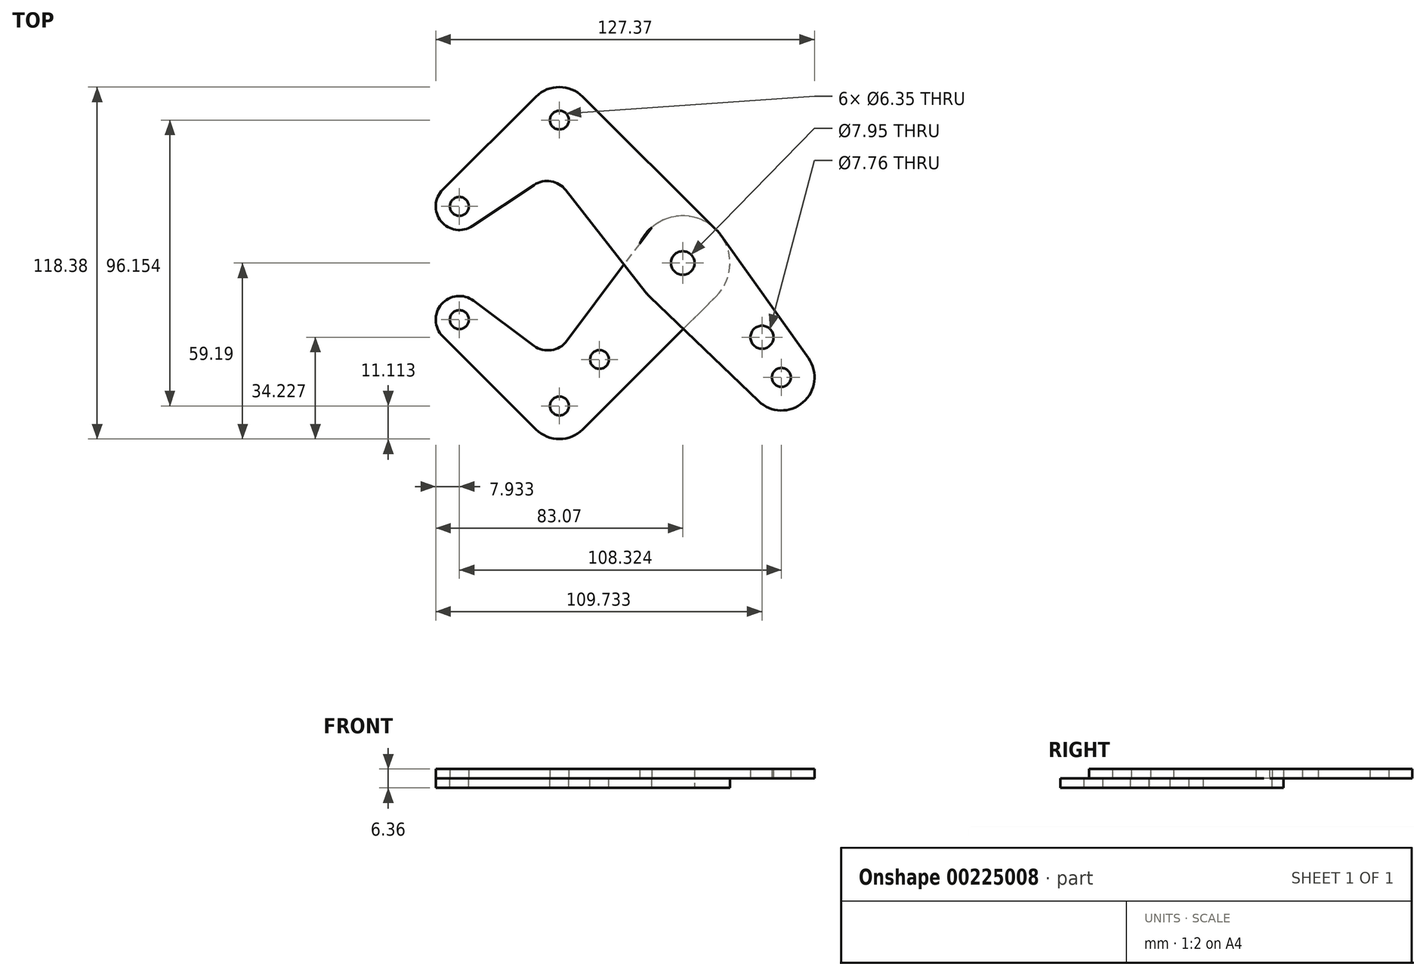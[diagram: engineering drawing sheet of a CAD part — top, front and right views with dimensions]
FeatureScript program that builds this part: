
annotation { "Feature Type Name" : "Feature", "Feature Type Description" : "" }
export const myFeature = defineFeature(function(context is Context, id is Id, definition is map)
    precondition{}
    {
        {
            var Q0;
            Q0=qCreatedBy(makeId("Top.planeOp"),FACE);
            var sketch = newSketch(context, id + "F0", { "sketchPlane" : qUnion([Q0])});
            skCircle(sketch, "E0", {"center": v(0, 0) * mm, "radius": 15.88 * mm});
            skCircle(sketch, "E1", {"center": v(0, 0) * mm, "radius": 3.98 * mm});
            skLineSegment(sketch, "E2", {"start": v(0, 0) * mm, "end": v(-41.48, 48.08) * mm, "construction": true});
            skCircle(sketch, "E3", {"center": v(-41.48, 48.08) * mm, "radius": 11.11 * mm});
            skLineSegment(sketch, "E4", {"start": v(-33.64, 55.95) * mm, "end": v(11.2, 11.24) * mm});
            skLineSegment(sketch, "E5", {"start": v(-41.48, 48.08) * mm, "end": v(-75.14, 19.04) * mm, "construction": true});
            skCircle(sketch, "E6", {"center": v(-75.14, 19.04) * mm, "radius": 7.94 * mm});
            skCircle(sketch, "E7", {"center": v(-41.48, 48.08) * mm, "radius": 3.18 * mm});
            skCircle(sketch, "E8", {"center": v(-75.14, 19.04) * mm, "radius": 3.18 * mm});
            skLineSegment(sketch, "E9", {"start": v(-80.74, 24.66) * mm, "end": v(-49.33, 55.95) * mm});
            skLineSegment(sketch, "E10", {"start": v(-70.74, 12.43) * mm, "end": v(-49.99, 26.24) * mm});
            skLineSegment(sketch, "E11", {"start": v(-12.5, -9.78) * mm, "end": v(-39.32, 24.52) * mm});
            skPoint(sketch, "E12.visualSharp", {"position": v(-43.86, 30.32) * mm});
            skArc(sketch, "E12.filletArc", {"start": v(-39.32, 24.52) * mm, "mid": v(-44.32, 27.47) * mm, "end": v(-49.99, 26.24) * mm});
            skLineSegment(sketch, "E13", {"start": v(0, 0) * mm, "end": v(33.19, -38.46) * mm, "construction": true});
            skCircle(sketch, "E14", {"center": v(0, 0) * mm, "radius": 3.18 * mm});
            skCircle(sketch, "E15", {"center": v(33.19, -38.46) * mm, "radius": 11.11 * mm});
            skCircle(sketch, "E16", {"center": v(33.19, -38.46) * mm, "radius": 3.18 * mm});
            skCircle(sketch, "E17", {"center": v(26.66, -24.96) * mm, "radius": 3.88 * mm});
            skLineSegment(sketch, "E18", {"start": v(12.94, 9.2) * mm, "end": v(42.24, -32.02) * mm});
            skLineSegment(sketch, "E19", {"start": v(-11, -11.45) * mm, "end": v(25.5, -46.48) * mm});
            skLineSegment(sketch, "E20", {"start": v(0, 0) * mm, "end": v(-41.48, -48.08) * mm, "construction": true});
            skCircle(sketch, "E21", {"center": v(-41.48, -48.08) * mm, "radius": 11.11 * mm});
            skCircle(sketch, "E22", {"center": v(-41.48, -48.08) * mm, "radius": 3.18 * mm});
            skCircle(sketch, "E23", {"center": v(-28, -32.44) * mm, "radius": 4.78 * mm});
            skLineSegment(sketch, "E24", {"start": v(-33.64, -55.95) * mm, "end": v(11.2, -11.24) * mm});
            skLineSegment(sketch, "E25", {"start": v(-41.48, -48.08) * mm, "end": v(-75.14, -19.04) * mm, "construction": true});
            skCircle(sketch, "E26", {"center": v(-75.14, -19.04) * mm, "radius": 7.94 * mm});
            skCircle(sketch, "E27", {"center": v(-75.14, -19.04) * mm, "radius": 3.18 * mm});
            skLineSegment(sketch, "E28", {"start": v(-80.74, -24.66) * mm, "end": v(-49.33, -55.95) * mm});
            skLineSegment(sketch, "E29", {"start": v(-10.37, 12.02) * mm, "end": v(-38.98, -26.2) * mm});
            skLineSegment(sketch, "E30", {"start": v(-70.4, -12.67) * mm, "end": v(-50.1, -27.8) * mm});
            skLineSegment(sketch, "E31.trimOffspring", {"start": v(-49.92, -40.8) * mm, "end": v(-50.38, -41.42) * mm});
            skLineSegment(sketch, "E32.trimOffspring", {"start": v(-34.84, -39.17) * mm, "end": v(-34.2, -39.64) * mm});
            skPoint(sketch, "E33.visualSharp", {"position": v(-43.73, -32.54) * mm});
            skArc(sketch, "E33.filletArc", {"start": v(-50.1, -27.8) * mm, "mid": v(-44.2, -29.3) * mm, "end": v(-38.98, -26.2) * mm});
            skLineSegment(sketch, "E34", {"start": v(-75.14, -19.04) * mm, "end": v(-75.14, 19.04) * mm, "construction": true});
            skCircle(sketch, "E35", {"center": v(-28, -32.44) * mm, "radius": 3.18 * mm});
            skSolve(sketch);
        }
        {
            var Q0;
            {var subQ0=sQuery(id+"F0.wireOp",EDGE,"E4");Q0=makeQuery(id+"F0.imprint","IMPRINT",FACE,{"disambiguationData":[TD([[makeQuery(id+"F0.imprint","IMPRINT",EDGE,{"derivedFrom":subQ0}),-1.0]])]});}
            var Q1;
            {var subQ0=sQuery(id+"F0.wireOp",EDGE,"E17");Q1=makeQuery(id+"F0.imprint","IMPRINT",FACE,{"disambiguationData":[TD([[makeQuery(id+"F0.imprint","IMPRINT",EDGE,{"derivedFrom":subQ0}),-1.0]])]});}
            var Q2;
            {var subQ0=sQuery(id+"F0.wireOp",EDGE,"E19");var subQ1=sQuery(id+"F0.wireOp",EDGE,"E0");var subQ2=makeQuery(id+"F0.imprint","INTERSECT",VERTEX,{"derivedFrom":[subQ1,subQ0]});Q2=makeQuery(id+"F0.imprint","IMPRINT",FACE,{"disambiguationData":[TD([[makeQuery(id+"F0.imprint","IMPRINT",EDGE,{"disambiguationData":[TD([[subQ2,-1.0]])],"derivedFrom":subQ1}),-1.0]])]});}
            var Q3;
            {var subQ0=sQuery(id+"F0.wireOp",EDGE,"E11");var subQ1=sQuery(id+"F0.wireOp",EDGE,"E0");var subQ2=makeQuery(id+"F0.imprint","INTERSECT",VERTEX,{"derivedFrom":[subQ1,subQ0]});Q3=makeQuery(id+"F0.imprint","IMPRINT",FACE,{"disambiguationData":[TD([[makeQuery(id+"F0.imprint","IMPRINT",EDGE,{"disambiguationData":[TD([[subQ2,1.0]])],"derivedFrom":subQ1}),-1.0]])]});}
            var Q4;
            Q4=makeQuery(id+"F0.imprint","IMPRINT",FACE,{"disambiguationData":[TD([[makeQuery(id+"F0.imprint","IMPRINT",EDGE,{"derivedFrom":sQuery(id+"F0.wireOp",EDGE,"E8")}),-1.0]])]});
            var Q5;
            Q5=makeQuery(id+"F0.imprint","IMPRINT",FACE,{"disambiguationData":[TD([[makeQuery(id+"F0.imprint","IMPRINT",EDGE,{"derivedFrom":sQuery(id+"F0.wireOp",EDGE,"E7")}),-1.0]])]});
            var Q6;
            Q6=makeQuery(id+"F0.imprint","IMPRINT",FACE,{"disambiguationData":[TD([[makeQuery(id+"F0.imprint","IMPRINT",EDGE,{"derivedFrom":sQuery(id+"F0.wireOp",EDGE,"E1")}),-1.0]])]});
            var Q7;
            Q7=makeQuery(id+"F0.imprint","IMPRINT",FACE,{"disambiguationData":[TD([[makeQuery(id+"F0.imprint","IMPRINT",EDGE,{"derivedFrom":sQuery(id+"F0.wireOp",EDGE,"E16")}),-1.0]])]});
            extrude(context, id + "F1", {"entities" : qUnion([Q0, Q1, Q2, Q3, Q4, Q5, Q6, Q7]), "depth" : 3.17 * mm});
        }
        {
            var Q0;
            Q0=makeQuery(id+"F0.imprint","IMPRINT",FACE,{"disambiguationData":[TD([[makeQuery(id+"F0.imprint","IMPRINT",EDGE,{"derivedFrom":sQuery(id+"F0.wireOp",EDGE,"E23")}),-1.0]])]});
            var Q1;
            {var subQ0=sQuery(id+"F0.wireOp",EDGE,"E19");var subQ1=sQuery(id+"F0.wireOp",EDGE,"E0");var subQ2=makeQuery(id+"F0.imprint","INTERSECT",VERTEX,{"derivedFrom":[subQ1,subQ0]});Q1=makeQuery(id+"F0.imprint","IMPRINT",FACE,{"disambiguationData":[TD([[makeQuery(id+"F0.imprint","IMPRINT",EDGE,{"disambiguationData":[TD([[subQ2,-1.0]])],"derivedFrom":subQ1}),-1.0]])]});}
            var Q2;
            {var subQ0=sQuery(id+"F0.wireOp",EDGE,"E11");var subQ1=sQuery(id+"F0.wireOp",EDGE,"E0");var subQ2=makeQuery(id+"F0.imprint","INTERSECT",VERTEX,{"derivedFrom":[subQ1,subQ0]});Q2=makeQuery(id+"F0.imprint","IMPRINT",FACE,{"disambiguationData":[TD([[makeQuery(id+"F0.imprint","IMPRINT",EDGE,{"disambiguationData":[TD([[subQ2,1.0]])],"derivedFrom":subQ1}),-1.0]])]});}
            var Q3;
            Q3=makeQuery(id+"F0.imprint","IMPRINT",FACE,{"disambiguationData":[TD([[makeQuery(id+"F0.imprint","IMPRINT",EDGE,{"derivedFrom":sQuery(id+"F0.wireOp",EDGE,"E1")}),-1.0]])]});
            var Q4;
            Q4=makeQuery(id+"F0.imprint","IMPRINT",FACE,{"disambiguationData":[TD([[makeQuery(id+"F0.imprint","IMPRINT",EDGE,{"derivedFrom":sQuery(id+"F0.wireOp",EDGE,"E23")}),1.0]])]});
            var Q5;
            Q5=makeQuery(id+"F0.imprint","IMPRINT",FACE,{"disambiguationData":[TD([[makeQuery(id+"F0.imprint","IMPRINT",EDGE,{"derivedFrom":sQuery(id+"F0.wireOp",EDGE,"E22")}),-1.0]])]});
            var Q6;
            Q6=makeQuery(id+"F0.imprint","IMPRINT",FACE,{"disambiguationData":[TD([[makeQuery(id+"F0.imprint","IMPRINT",EDGE,{"derivedFrom":sQuery(id+"F0.wireOp",EDGE,"E27")}),-1.0]])]});
            extrude(context, id + "F2", {"entities" : qUnion([Q0, Q1, Q2, Q3, Q4, Q5, Q6]), "operationType" : NewBodyOperationType.ADD, "oppositeDirection" : true, "depth" : 3.17 * mm});
        }
    });
